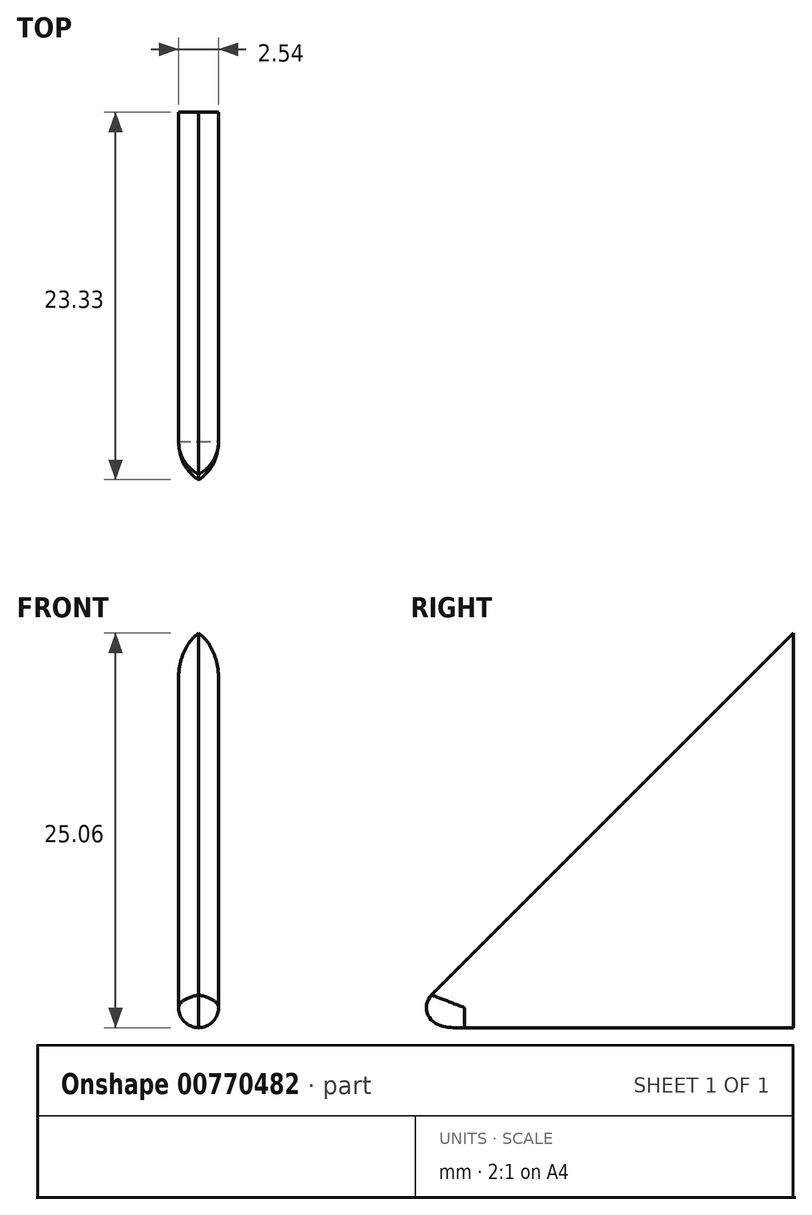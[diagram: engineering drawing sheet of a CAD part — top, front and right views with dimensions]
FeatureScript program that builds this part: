
annotation { "Feature Type Name" : "Feature", "Feature Type Description" : "" }
export const myFeature = defineFeature(function(context is Context, id is Id, definition is map)
    precondition{}
    {
        {
            var Q0;
            Q0=qCreatedBy(makeId("Top.planeOp"),FACE);
            var sketch = newSketch(context, id + "F0", { "sketchPlane" : qUnion([Q0])});
            skLineSegment(sketch, "E0.bottom", {"start": v(-1.27, 12.7) * mm, "end": v(1.27, 12.7) * mm});
            skLineSegment(sketch, "E0.top", {"start": v(-1.27, -12.7) * mm, "end": v(1.27, -12.7) * mm});
            skLineSegment(sketch, "E0.left", {"start": v(-1.27, 12.7) * mm, "end": v(-1.27, -12.7) * mm});
            skLineSegment(sketch, "E0.right", {"start": v(1.27, 12.7) * mm, "end": v(1.27, -12.7) * mm});
            skPoint(sketch, "E0.middle", {"position": v(0, 0) * mm});
            skSolve(sketch);
        }
        {
            var Q0;
            Q0=makeQuery(id+"F0.imprint","IMPRINT",FACE,{"disambiguationData":[TD([[makeQuery(id+"F0.imprint","IMPRINT",EDGE,{"derivedFrom":sQuery(id+"F0.wireOp",EDGE,"E0.bottom")}),-1.0]])]});
            extrude(context, id + "F1", {"entities" : qUnion([Q0]), "depth" : 25.4 * mm, "offsetDistance" : 25.4 * mm});
        }
        {
            var Q0;
            Q0=makeQuery(id+"F1.opExtrude","CAP_EDGE",EDGE,{"disambiguationData":[OSD([sQuery(id+"F0.wireOp",EDGE,"E0.top")])],"isStart":false});
            chamfer(context, id + "F2", {"entities" : qUnion([Q0]), "width" : 25.4 * mm, "tangentPropagation" : true});
        }
        {
            var Q0;
            Q0=makeQuery(id+"F2.opChamfer","BLEND_EDGE",EDGE,{"blendedFrom":[makeQuery(id+"F1.opExtrude","CAP_EDGE",EDGE,{"disambiguationData":[OSD([sQuery(id+"F0.wireOp",EDGE,"E0.top")])],"isStart":false}),makeQuery(id+"F1.opExtrude","SWEPT_FACE",FACE,{"disambiguationData":[OSD([sQuery(id+"F0.wireOp",EDGE,"E0.right")])]})],"blendedInto":[makeQuery(id+"F1.opExtrude","SWEPT_FACE",FACE,{"disambiguationData":[OSD([sQuery(id+"F0.wireOp",EDGE,"E0.right")])]})]});
            var Q1;
            Q1=makeQuery(id+"F2.opChamfer","BLEND_EDGE",EDGE,{"blendedFrom":[makeQuery(id+"F1.opExtrude","CAP_EDGE",EDGE,{"disambiguationData":[OSD([sQuery(id+"F0.wireOp",EDGE,"E0.top")])],"isStart":false}),makeQuery(id+"F1.opExtrude","SWEPT_FACE",FACE,{"disambiguationData":[OSD([sQuery(id+"F0.wireOp",EDGE,"E0.left")])]})],"blendedInto":[makeQuery(id+"F1.opExtrude","SWEPT_FACE",FACE,{"disambiguationData":[OSD([sQuery(id+"F0.wireOp",EDGE,"E0.left")])]})]});
            fillet(context, id + "F3", {"entities" : qUnion([Q0, Q1]), "radius" : 2.3 * mm, "tangentPropagation" : true, "allowEdgeOverflow" : false});
        }
        {
            var Q0;
            Q0=makeQuery(id+"F1.opExtrude","CAP_EDGE",EDGE,{"disambiguationData":[OSD([sQuery(id+"F0.wireOp",EDGE,"E0.right")])],"isStart":true});
            var Q1;
            Q1=makeQuery(id+"F1.opExtrude","CAP_EDGE",EDGE,{"disambiguationData":[OSD([sQuery(id+"F0.wireOp",EDGE,"E0.left")])],"isStart":true});
            fillet(context, id + "F4", {"entities" : qUnion([Q0, Q1]), "radius" : 1.27 * mm, "tangentPropagation" : true, "allowEdgeOverflow" : false});
        }
    });
